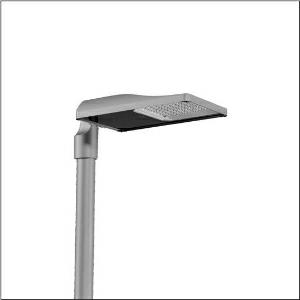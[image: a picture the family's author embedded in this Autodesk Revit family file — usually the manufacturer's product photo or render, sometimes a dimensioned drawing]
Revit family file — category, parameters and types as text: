
# Revit family: streetlight_sl_31_midi___pl52_5xh7h4aa08ma_ed53
name_source: partatom
category: Lighting Fixtures
units: mm (PartAtom-declared; Revit-internal decimal feet)

## family parameters
Cut with Voids When Loaded = No
Host = Face
Light Source = No
Part Type = Normal
Room Calculation Point = No
Round Connector Dimension = Use Diameter
Shared = No

## types (1)
- --- (1 x LED, 19840 lm, 145.3 W, 4000K)
    Apparent Load = 145 VA
    CIE Flux Codes = 27 59 98 100 100
    Color Rendering = 70
    Color Temperature = 4000K
    Default Elevation = 1800 mm
    Description = Streetlight SL 31 midi Easy mast luminaire for post-top, side-entry; light control with lens of PMMA; light distribution: PL52, direct asymmetric distribution, for standard-compliant lighting for roads and squares; LED: luminous flux: 19.840lm, light colour: 740, colour temperature: 4000K; luminous efficacy: 136,5lm/W; control: pre-setting: linear dimming characteristic, flexible luminous flux parameterisation, time-dependent luminous flux control, constant luminous flux control, power reduction, intelligent temperature release in ECG and LED module, overheat protection; luminaire housing, of diecast aluminium, SITECO metallic grey (DB 702S), corrosivity category C5 high according to DIN EN ISO 12944; cover of toughened safety glass, transparent, opened without tools; mast flange of diecast aluminium, SITECO metallic grey (DB 702S), spigot size: 76/60mm, mast flange included unmounted; cable length: 10,5m, connection cable pre-assembled; mains connection: 220..240V, AC, 50/60Hz; power consumption (at start of service life): 145,3W / (at end of service life): 161,8W / (with reduced operation 50%): 61,1W; protection rating (complete): IP66; insulation class (complete): insulation class II (safety insulation); impact resistance: IK10; certification: CE, ENEC, ENEC+, VDE, UKCA; permissible operating ambient temperature for outdoor applications: -40..+50°C; packaging unit: 1 piece

Light Distribution: PL52
    Height = 79 mm
    Lamp = 1 x LED
    Lamp Light Flux = 19840 lm
    Lamp Power = 145.3 W
    Lamp count = 1
    Length = 577 mm
    Luminous efficacy = 137 lm/W
    Manufacturer = Siteco
    ModVariant = No
    Model = 5XH7H4AA08MA
    Number of Poles = 1
    OnlyDefault = Yes
    Power Factor = 1
    Product Name = Streetlight SL 31 midi | PL52
    Product group = mast luminaire | pylon top
    ProductGroupID = 6100
    Protection Class = Protection class II
    Protection Degree = IP 66
    RLX_Detail_Level = 1
    RLX_Emergency_Light_Flux = 0 lm
    RLX_Emergency_Type = 0
    RLX_Emergency_Type_DB = No
    RlxData = <blob elided: 52409 chars, md5=ded172a8>
    Socket = socket
    Standby Power = 0 W
    System Light Flux = 19841 lm
    System Power = 145 W
    Type Comments = factory setting: luminous flux: 100 % | dim-lin: 254 | 747 mA
    Type Image = l_1300317.jpg
    URL = http://relux.com
    VarID = @adj_064271
    Voltage = 0 V
    Weight = 0.00 kg
    Width = 362 mm

## geometry (parser evidence)
native form markers: Blend x4, Sweep x9
no freeform markers — native parametric forms only
